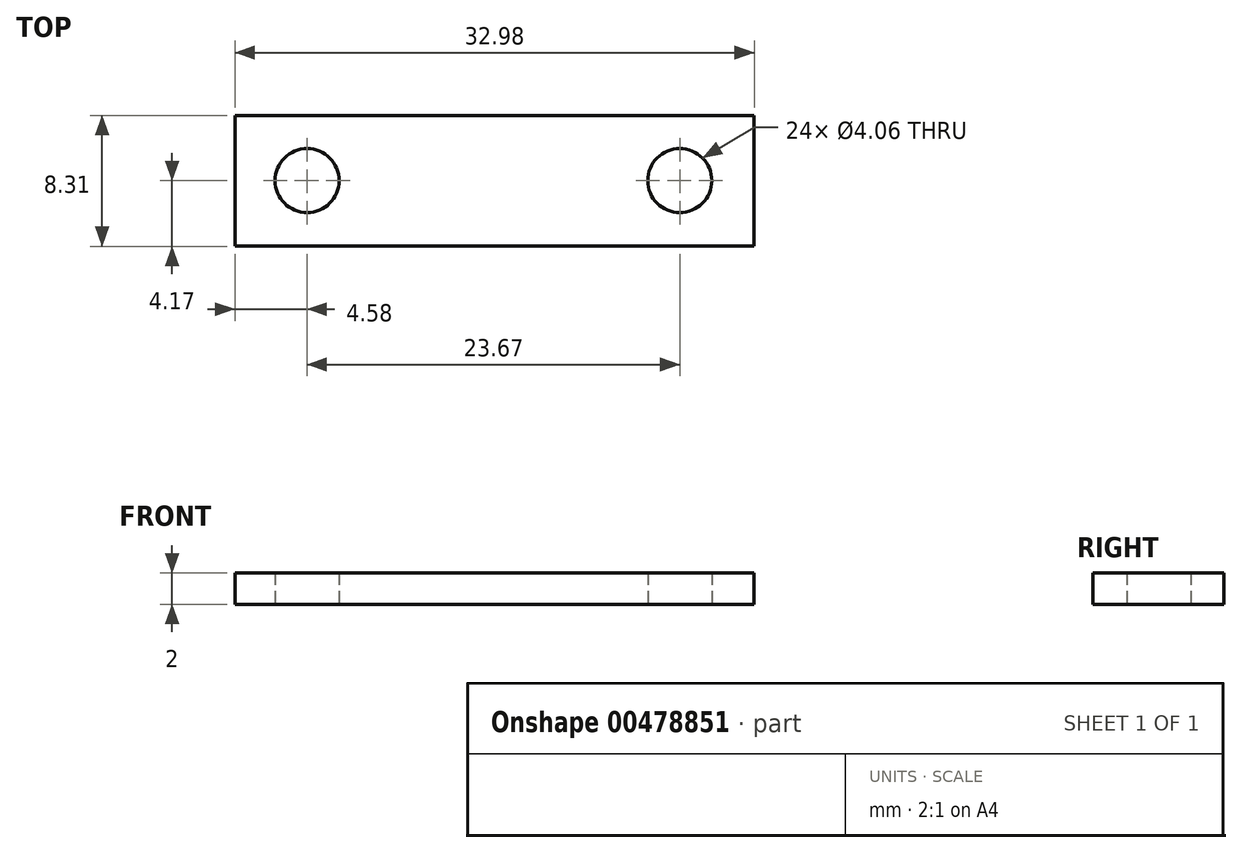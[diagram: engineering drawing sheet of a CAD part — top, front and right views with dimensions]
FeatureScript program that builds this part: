
annotation { "Feature Type Name" : "Feature", "Feature Type Description" : "" }
export const myFeature = defineFeature(function(context is Context, id is Id, definition is map)
    precondition{}
    {
        {
            var Q0;
            Q0=qCreatedBy(makeId("Top.planeOp"),FACE);
            var sketch = newSketch(context, id + "F0", { "sketchPlane" : qUnion([Q0])});
            skCircle(sketch, "E0", {"center": v(0, 0) * mm, "radius": 2.03 * mm});
            skCircle(sketch, "E1", {"center": v(23.67, 0) * mm, "radius": 2.03 * mm});
            skLineSegment(sketch, "E2.bottom", {"start": v(-4.58, 4.14) * mm, "end": v(28.4, 4.14) * mm});
            skLineSegment(sketch, "E2.top", {"start": v(-4.58, -4.17) * mm, "end": v(28.4, -4.17) * mm});
            skLineSegment(sketch, "E2.left", {"start": v(-4.58, 4.14) * mm, "end": v(-4.58, -4.17) * mm});
            skLineSegment(sketch, "E2.right", {"start": v(28.4, 4.14) * mm, "end": v(28.4, -4.17) * mm});
            skSolve(sketch);
        }
        {
            var Q0;
            Q0=makeQuery(id+"F0.imprint","IMPRINT",FACE,{"disambiguationData":[TD([[makeQuery(id+"F0.imprint","IMPRINT",EDGE,{"derivedFrom":sQuery(id+"F0.wireOp",EDGE,"E0")}),-1.0]])]});
            extrude(context, id + "F1", {"entities" : qUnion([Q0]), "depth" : 2 * mm});
        }
    });
